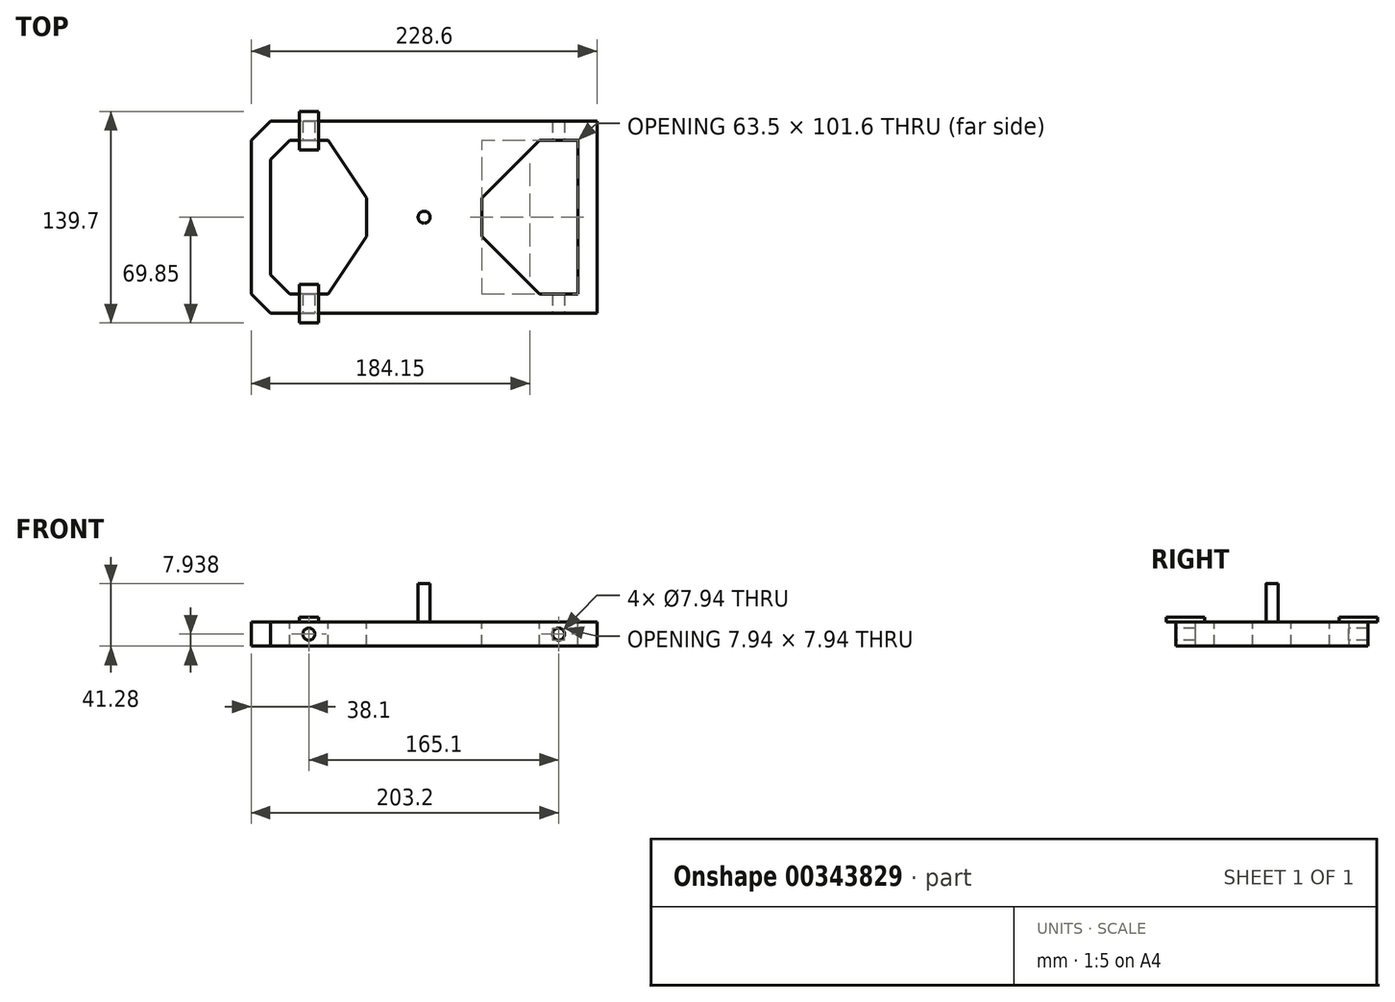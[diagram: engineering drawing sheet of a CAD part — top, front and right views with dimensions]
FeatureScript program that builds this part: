
annotation { "Feature Type Name" : "Feature", "Feature Type Description" : "" }
export const myFeature = defineFeature(function(context is Context, id is Id, definition is map)
    precondition{}
    {
        {
            var Q0;
            Q0=qCreatedBy(makeId("Top.planeOp"),FACE);
            var sketch = newSketch(context, id + "F0", { "sketchPlane" : qUnion([Q0])});
            skLineSegment(sketch, "E0", {"start": v(-114.3, 50.8) * mm, "end": v(-114.3, -50.8) * mm});
            skLineSegment(sketch, "E1", {"start": v(-114.3, -50.8) * mm, "end": v(-101.6, -63.5) * mm});
            skLineSegment(sketch, "E2", {"start": v(-101.6, -63.5) * mm, "end": v(114.3, -63.5) * mm});
            skLineSegment(sketch, "E3", {"start": v(114.3, -63.5) * mm, "end": v(114.3, 63.5) * mm});
            skLineSegment(sketch, "E4", {"start": v(114.3, 63.5) * mm, "end": v(-101.6, 63.5) * mm});
            skLineSegment(sketch, "E5", {"start": v(-101.6, 63.5) * mm, "end": v(-114.3, 50.8) * mm});
            skSolve(sketch);
        }
        {
            var Q0;
            Q0 = qSketchRegion(id + "F0", true);
            extrude(context, id + "F1", {"entities" : qUnion([Q0]), "depth" : 15.88 * mm});
        }
        {
            var Q0;
            Q0=qCreatedBy(makeId("Front.planeOp"),FACE);
            var sketch = newSketch(context, id + "F2", { "sketchPlane" : qUnion([Q0])});
            skCircle(sketch, "E6", {"center": v(-76.2, 7.94) * mm, "radius": 3.97 * mm});
            skCircle(sketch, "E7", {"center": v(88.9, 7.94) * mm, "radius": 3.97 * mm});
            skSolve(sketch);
        }
        {
            var Q0;
            Q0 = qSketchRegion(id + "F2", true);
            extrude(context, id + "F3", {"entities" : qUnion([Q0]), "operationType" : NewBodyOperationType.REMOVE, "endBound" : BoundingType.SYMMETRIC, "oppositeDirection" : true, "depth" : 254 * mm});
        }
        {
            var Q0;
            Q0=makeQuery(id+"F1.opExtrude","CAP_FACE",FACE,{"disambiguationData":[OSD([sQuery(id+"F0.wireOp",EDGE,"E0"),sQuery(id+"F0.wireOp",EDGE,"E1"),sQuery(id+"F0.wireOp",EDGE,"E2"),sQuery(id+"F0.wireOp",EDGE,"E3"),sQuery(id+"F0.wireOp",EDGE,"E4"),sQuery(id+"F0.wireOp",EDGE,"E5")])],"isStart":false});
            var sketch = newSketch(context, id + "F4", { "sketchPlane" : qUnion([Q0])});
            skLineSegment(sketch, "E8", {"start": v(38.1, 12.7) * mm, "end": v(38.1, -12.7) * mm});
            skLineSegment(sketch, "E9", {"start": v(38.1, -12.7) * mm, "end": v(76.2, -50.8) * mm});
            skLineSegment(sketch, "E10", {"start": v(76.2, -50.8) * mm, "end": v(101.6, -50.8) * mm});
            skLineSegment(sketch, "E11", {"start": v(101.6, -50.8) * mm, "end": v(101.6, 50.8) * mm});
            skLineSegment(sketch, "E12", {"start": v(101.6, 50.8) * mm, "end": v(76.2, 50.8) * mm});
            skLineSegment(sketch, "E13", {"start": v(76.2, 50.8) * mm, "end": v(38.1, 12.7) * mm});
            skSolve(sketch);
        }
        {
            var Q0;
            Q0=makeQuery(id+"F4.imprint","IMPRINT",FACE,{"disambiguationData":[TD([[makeQuery(id+"F4.imprint","IMPRINT",EDGE,{"derivedFrom":sQuery(id+"F4.wireOp",EDGE,"E8")}),1.0]])]});
            extrude(context, id + "F5", {"entities" : qUnion([Q0]), "operationType" : NewBodyOperationType.REMOVE, "endBound" : BoundingType.THROUGH_ALL, "oppositeDirection" : true, "depth" : 25.4 * mm});
        }
        {
            var Q0;
            Q0=makeQuery(id+"F1.opExtrude","CAP_FACE",FACE,{"disambiguationData":[OSD([sQuery(id+"F0.wireOp",EDGE,"E0"),sQuery(id+"F0.wireOp",EDGE,"E1"),sQuery(id+"F0.wireOp",EDGE,"E2"),sQuery(id+"F0.wireOp",EDGE,"E3"),sQuery(id+"F0.wireOp",EDGE,"E4"),sQuery(id+"F0.wireOp",EDGE,"E5")])],"isStart":false});
            var sketch = newSketch(context, id + "F6", { "sketchPlane" : qUnion([Q0])});
            skLineSegment(sketch, "E14", {"start": v(-38.1, 12.7) * mm, "end": v(-38.1, -12.7) * mm});
            skLineSegment(sketch, "E15", {"start": v(-38.1, -12.7) * mm, "end": v(-63.5, -50.8) * mm});
            skLineSegment(sketch, "E16", {"start": v(-63.5, -50.8) * mm, "end": v(-88.9, -50.8) * mm});
            skLineSegment(sketch, "E17", {"start": v(-88.9, -50.8) * mm, "end": v(-101.6, -38.1) * mm});
            skLineSegment(sketch, "E18", {"start": v(-101.6, -38.1) * mm, "end": v(-101.6, 38.1) * mm});
            skLineSegment(sketch, "E19", {"start": v(-101.6, 38.1) * mm, "end": v(-88.9, 50.8) * mm});
            skLineSegment(sketch, "E20", {"start": v(-88.9, 50.8) * mm, "end": v(-63.5, 50.8) * mm});
            skLineSegment(sketch, "E21", {"start": v(-63.5, 50.8) * mm, "end": v(-38.1, 12.7) * mm});
            skSolve(sketch);
        }
        {
            var Q0;
            Q0 = qSketchRegion(id + "F6", true);
            extrude(context, id + "F7", {"entities" : qUnion([Q0]), "operationType" : NewBodyOperationType.REMOVE, "oppositeDirection" : true, "depth" : 25.4 * mm});
        }
        {
            var Q0;
            Q0=makeQuery(id+"F1.opExtrude","CAP_FACE",FACE,{"disambiguationData":[OSD([sQuery(id+"F0.wireOp",EDGE,"E0"),sQuery(id+"F0.wireOp",EDGE,"E1"),sQuery(id+"F0.wireOp",EDGE,"E2"),sQuery(id+"F0.wireOp",EDGE,"E3"),sQuery(id+"F0.wireOp",EDGE,"E4"),sQuery(id+"F0.wireOp",EDGE,"E5")])],"isStart":false});
            var sketch = newSketch(context, id + "F8", { "sketchPlane" : qUnion([Q0])});
            skCircle(sketch, "E22", {"center": v(0, 0) * mm, "radius": 3.97 * mm});
            skSolve(sketch);
        }
        {
            var Q0;
            Q0 = qSketchRegion(id + "F8", true);
            extrude(context, id + "F9", {"entities" : qUnion([Q0]), "operationType" : NewBodyOperationType.ADD, "depth" : 25.4 * mm});
        }
        {
            var Q0;
            Q0=makeQuery(id+"F1.opExtrude","CAP_FACE",FACE,{"disambiguationData":[OSD([sQuery(id+"F0.wireOp",EDGE,"E0"),sQuery(id+"F0.wireOp",EDGE,"E1"),sQuery(id+"F0.wireOp",EDGE,"E2"),sQuery(id+"F0.wireOp",EDGE,"E3"),sQuery(id+"F0.wireOp",EDGE,"E4"),sQuery(id+"F0.wireOp",EDGE,"E5")])],"isStart":false});
            var sketch = newSketch(context, id + "F10", { "sketchPlane" : qUnion([Q0])});
            skLineSegment(sketch, "E23.bottom", {"start": v(-82.55, 44.45) * mm, "end": v(-69.85, 44.45) * mm});
            skLineSegment(sketch, "E23.top", {"start": v(-82.55, 69.85) * mm, "end": v(-69.85, 69.85) * mm});
            skLineSegment(sketch, "E23.left", {"start": v(-82.55, 44.45) * mm, "end": v(-82.55, 69.85) * mm});
            skLineSegment(sketch, "E23.right", {"start": v(-69.85, 44.45) * mm, "end": v(-69.85, 69.85) * mm});
            skLineSegment(sketch, "E24.bottom", {"start": v(-82.55, -44.45) * mm, "end": v(-69.85, -44.45) * mm});
            skLineSegment(sketch, "E24.top", {"start": v(-82.55, -69.85) * mm, "end": v(-69.85, -69.85) * mm});
            skLineSegment(sketch, "E24.left", {"start": v(-82.55, -44.45) * mm, "end": v(-82.55, -69.85) * mm});
            skLineSegment(sketch, "E24.right", {"start": v(-69.85, -44.45) * mm, "end": v(-69.85, -69.85) * mm});
            skSolve(sketch);
        }
        {
            var Q0;
            Q0 = qSketchRegion(id + "F10", true);
            extrude(context, id + "F11", {"entities" : qUnion([Q0]), "operationType" : NewBodyOperationType.ADD, "depth" : 3.17 * mm});
        }
    });
